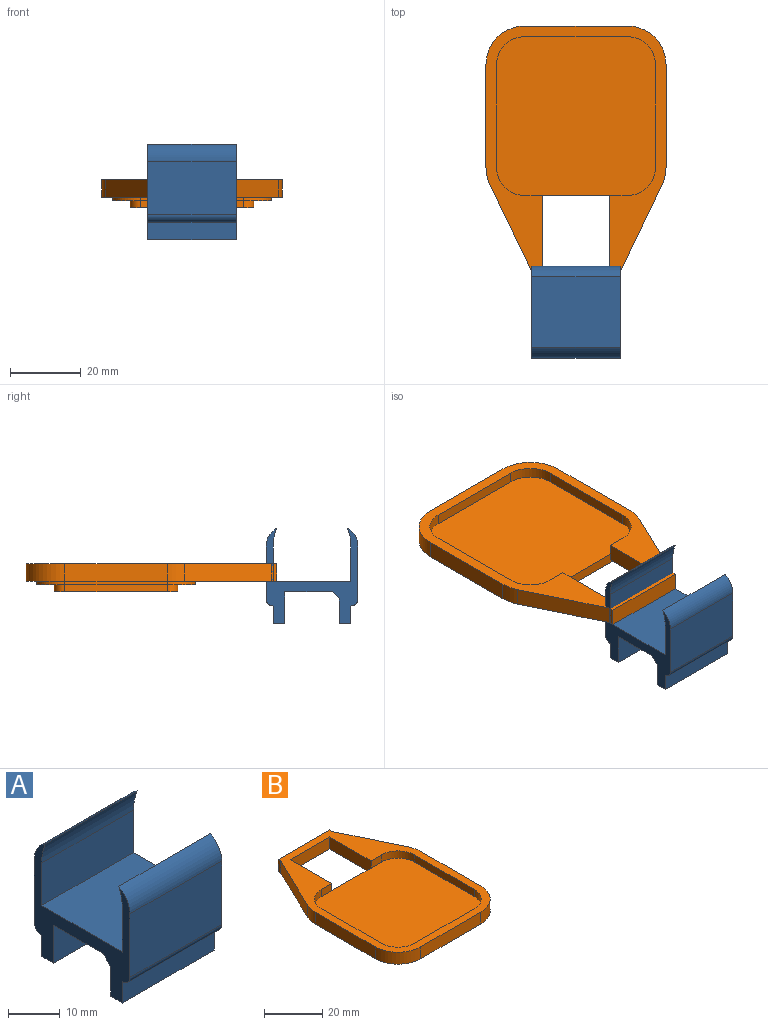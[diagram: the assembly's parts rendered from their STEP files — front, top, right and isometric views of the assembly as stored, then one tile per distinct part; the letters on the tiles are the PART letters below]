
ASSEMBLY  parts=2 mates=1
PART A: 21 faces, bbox 25x26x27 mm
  f0: plane 25x15mm, normal (0,1,0), area 375mm2, adj f1,f16,f17,f20
  f1: cylinder r=5.67mm len=25mm, axis (-1,0,0), area 153.1mm2, adj f0,f2,f16,f17
  f2: cylinder r=13mm len=25mm, axis (-1,0,0), area 128.3mm2, adj f1,f3,f16,f17
  f3: plane 25x10mm, normal (0,-1,0), area 250mm2, adj f2,f4,f16,f17
  f4: plane 25x22mm, normal (0,0,1), area 550mm2, adj f3,f5,f16,f17
  f5: plane 25x10mm, normal (0,1,0), area 250mm2, adj f4,f6,f16,f17
  f6: cylinder r=13mm len=25mm, axis (-1,0,0), area 128.3mm2, adj f5,f7,f16,f17
  f7: cylinder r=5.67mm len=25mm, axis (-1,0,0), area 153.1mm2, adj f6,f8,f16,f17
  f8: plane 25x15mm, normal (0,-1,0), area 375mm2, adj f7,f16,f17,f19
  f9: plane 25x5mm, normal (0,-1,0), area 125mm2, adj f10,f16,f17,f19
  f10: plane 25x3.25mm, normal (0,0,-1), area 81.2mm2, adj f9,f11,f16,f17
  f11: plane 25x7mm, normal (0,1,0), area 175mm2, adj f10,f16,f17,f18
  f12: plane 25x13.5mm, normal (0,0,-1), area 337.5mm2, adj f13,f16,f17,f18
  f13: plane 25x9mm, normal (0,-1,0), area 225mm2, adj f12,f14,f16,f17
  f14: plane 25x3.25mm, normal (0,0,-1), area 81.2mm2, adj f13,f15,f16,f17
  f15: plane 25x5mm, normal (0,1,0), area 125mm2, adj f14,f16,f17,f20
  f16: plane 27x26mm, normal (1,0,0), area 207.4mm2, adj f0,f1,f2,f3,f4,f5,f6,f7
  f17: plane 27x26mm, normal (-1,0,0), area 207.4mm2, adj f0,f1,f2,f3,f4,f5,f6,f7
  f18: plane 25x2mm, normal (0,0.71,-0.71), area 70.7mm2, adj f11,f12,f16,f17
  f19: cylinder r=2mm len=25mm, axis (-1,0,0), area 78.5mm2, adj f8,f9,f16,f17
  f20: cylinder r=2mm len=25mm, axis (-1,0,0), area 78.5mm2, adj f0,f15,f16,f17
PART B: 46 faces, bbox 51x71x8 mm
  f0: plane 20x5mm, normal (-1,0,0), area 100mm2, adj f1,f24,f25,f26,f27
  f1: plane 5x3mm, normal (0,-1,0), area 15mm2, adj f0,f2,f25,f36
  f2: cylinder r=8mm len=8mm, axis (0,0,-1), area 37.7mm2, adj f1,f3,f25,f36
  f3: plane 29x3mm, normal (-1,0,0), area 87mm2, adj f2,f4,f25,f36
  f4: cylinder r=8mm len=8mm, axis (0,0,-1), area 37.7mm2, adj f3,f5,f25,f36
  f5: plane 29x3mm, normal (0,1,0), area 87mm2, adj f4,f6,f25,f36
  f6: cylinder r=8mm len=8mm, axis (0,0,-1), area 37.7mm2, adj f5,f7,f25,f36
  f7: plane 29x3mm, normal (1,0,0), area 87mm2, adj f6,f8,f25,f36
  f8: cylinder r=8mm len=8mm, axis (0,0,-1), area 37.7mm2, adj f7,f9,f25,f36
  f9: plane 5x3mm, normal (0,-1,0), area 15mm2, adj f8,f10,f25,f36
  f10: plane 20x5mm, normal (1,0,0), area 100mm2, adj f9,f24,f25,f26,f27
  f11: cylinder r=11mm len=5mm, axis (0,0,-1), area 24.7mm2, adj f12,f23,f25,f26
  f12: plane 24.73x11.91mm, normal (0.9,0.43,0), area 137.2mm2, adj f11,f13,f25,f26
  f13: plane 5x1.5mm, normal (1,0,0), area 7.5mm2, adj f12,f14,f25,f26
  f14: plane 25x5mm, normal (0,1,0), area 125mm2, adj f13,f15,f25,f26
  f15: plane 5x1.5mm, normal (-1,0,0), area 7.5mm2, adj f14,f16,f25,f26
  f16: plane 5x0.07mm, normal (0,1,0), area 0.3mm2, adj f15,f17,f25,f26
  f17: plane 24.75x11.86mm, normal (-0.9,0.43,0), area 137.2mm2, adj f16,f18,f25,f26
  f18: cylinder r=11mm len=5mm, axis (0,0,-1), area 24.6mm2, adj f17,f19,f25,f26
  f19: plane 29x5mm, normal (-1,0,0), area 145mm2, adj f18,f20,f25,f26
  f20: cylinder r=11mm len=11mm, axis (0,0,-1), area 86.4mm2, adj f19,f21,f25,f26
  f21: plane 29x5mm, normal (0,-1,0), area 145mm2, adj f20,f22,f25,f26
  f22: cylinder r=11mm len=11mm, axis (0,0,-1), area 86.4mm2, adj f21,f23,f25,f26
  f23: plane 29x5mm, normal (1,0,0), area 145mm2, adj f11,f22,f25,f26
  f24: plane 19x5mm, normal (0,-1,0), area 95mm2, adj f0,f10,f25,f26
  f25: plane 71x51mm, normal (0,0,1), area 829mm2, adj f0,f1,f2,f3,f4,f5,f6,f7
  f26: plane 71x51mm, normal (0,0,-1), area 829mm2, adj f0,f10,f11,f12,f13,f14,f15,f16
  f27: plane 29x3mm, normal (0,1,0), area 67mm2, adj f0,f10,f26,f28,f34,f35,f36
  f28: cylinder r=8mm len=8mm, axis (0,0,1), area 12.6mm2, adj f26,f27,f29,f35
  f29: plane 29x1mm, normal (-1,0,0), area 29mm2, adj f26,f28,f30,f35
  f30: cylinder r=8mm len=8mm, axis (0,0,1), area 12.6mm2, adj f26,f29,f31,f35
  f31: plane 29x1mm, normal (0,-1,0), area 29mm2, adj f26,f30,f32,f35
  f32: cylinder r=8mm len=8mm, axis (0,0,1), area 12.6mm2, adj f26,f31,f33,f35
  f33: plane 29x1mm, normal (1,0,0), area 29mm2, adj f26,f32,f34,f35
  f34: cylinder r=8mm len=8mm, axis (0,0,1), area 12.6mm2, adj f26,f27,f33,f35
  f35: plane 45x45mm, normal (0,0,-1), area 752.8mm2, adj f27,f28,f29,f30,f31,f32,f33,f34
  f36: plane 45x45mm, normal (0,0,1), area 1970.1mm2, adj f1,f2,f3,f4,f5,f6,f7,f8
  f37: plane 35x35mm, normal (0,0,-1), area 1217.3mm2, adj f38,f39,f40,f41,f42,f43,f44,f45
  f38: cylinder r=3mm len=3mm, axis (0,0,1), area 9.4mm2, adj f35,f37,f42,f45
  f39: cylinder r=3mm len=3mm, axis (0,0,1), area 9.4mm2, adj f35,f37,f42,f43
  f40: cylinder r=3mm len=3mm, axis (0,0,1), area 9.4mm2, adj f35,f37,f43,f44
  f41: cylinder r=3mm len=3mm, axis (0,0,1), area 9.4mm2, adj f35,f37,f44,f45
  f42: plane 29x2mm, normal (1,0,0), area 58mm2, adj f35,f37,f38,f39
  f43: plane 29x2mm, normal (0,-1,0), area 58mm2, adj f35,f37,f39,f40
  f44: plane 29x2mm, normal (-1,0,0), area 58mm2, adj f35,f37,f40,f41
  f45: plane 29x2mm, normal (0,1,0), area 58mm2, adj f35,f37,f38,f41
PLACE A t=(-0.29,-4.66,0)mm
PLACE B rot(axis=(0,0,1),180deg) t=(12.21,50.84,5)mm
MATE fastened B.f24 <-> A.f0  axis (0,1,0) through (12.21,8.34,5.5)mm
